# Revit family: НЕBАТОМ_Диффузор VO, версия 1
name_source: partatom
category: Воздухораспределители
revit_build: Autodesk Revit 2017 (Build: 20170118_1100(x64)
units: mm (PartAtom-declared; Revit-internal decimal feet)

## family parameters
Всегда вертикально = Да
На основе рабочей плоскости = Нет
Общий = Нет
При загрузке вырезать с полостями = Нет
Размер круглого соединителя = Использовать диаметр
Тип детали = Нормальный
Точка расчета площади = Нет

## types (11) — shared parameters
ADSK_Единица измерения = шт.
ADSK_Завод-изготовитель = НЕВАТОМ
ADSK_Количество = 1
ADSK_Материал наименование = Оцинкованная сталь
ADSK_Наименование = Диффузор
Nevatom_URL = https://t.me

## per-type parameters (varying)
| type | ADSK_Марка | D | D1 | Dnf | Dnv | L | R1 | R2 | R3 | R4 |
| Диффузор VO №6,3 | VO-630/800 | 630 мм | 800 мм | 864 мм | 730 мм | 420 мм | 432 мм | 400 мм | 315 мм | 365 мм |
| Диффузор VO №4,0 | VO-400/500 | 400 мм | 500 мм | 550 мм | 480 мм | 289 мм | 275 мм | 250 мм | 200 мм | 240 мм |
| Диффузор VO №4,5 | VO-450/560 | 450 мм | 560 мм | 610 мм | 530 мм | 308 мм | 305 мм | 280 мм | 225 мм | 265 мм |
| Диффузор VO №5,0 | VO-500/630 | 500 мм | 630 мм | 680 мм | 590 мм | 345 мм | 340 мм | 315 мм | 250 мм | 295 мм |
| Диффузор VO №5,6 | VO-560/710 | 560 мм | 710 мм | 790 мм | 650 мм | 382 мм | 395 мм | 355 мм | 280 мм | 325 мм |
| Диффузор VO №7,1 | VO-710/900 | 710 мм | 900 мм | 964 мм | 810 мм | 457 мм | 482 мм | 450 мм | 355 мм | 405 мм |
| Диффузор VO №8,0 | VO-800/1000 | 800 мм | 1000 мм | 1080 мм | 900 мм | 476 мм | 540 мм | 500 мм | 400 мм | 450 мм |
| Диффузор VO №9,0 | VO-900/1120 | 900 мм | 1120 мм | 1184 мм | 1010 мм | 514 мм | 592 мм | 560 мм | 450 мм | 505 мм |
| Диффузор VO №10 | VO-1000/1250 | 1000 мм | 1250 мм | 1330 мм | 1100 мм | 570 мм | 665 мм | 625 мм | 500 мм | 550 мм |
| Диффузор VO №11,2 | VO-1120/1400 | 1120 мм | 1400 мм | 1480 мм | 1230 мм | 626 мм | 740 мм | 700 мм | 560 мм | 615 мм |
| Диффузор VO №12,5 | VO-1250/1600 | 1250 мм | 1600 мм | 1680 мм | 1360 мм | 756 мм | 840 мм | 800 мм | 625 мм | 680 мм |
